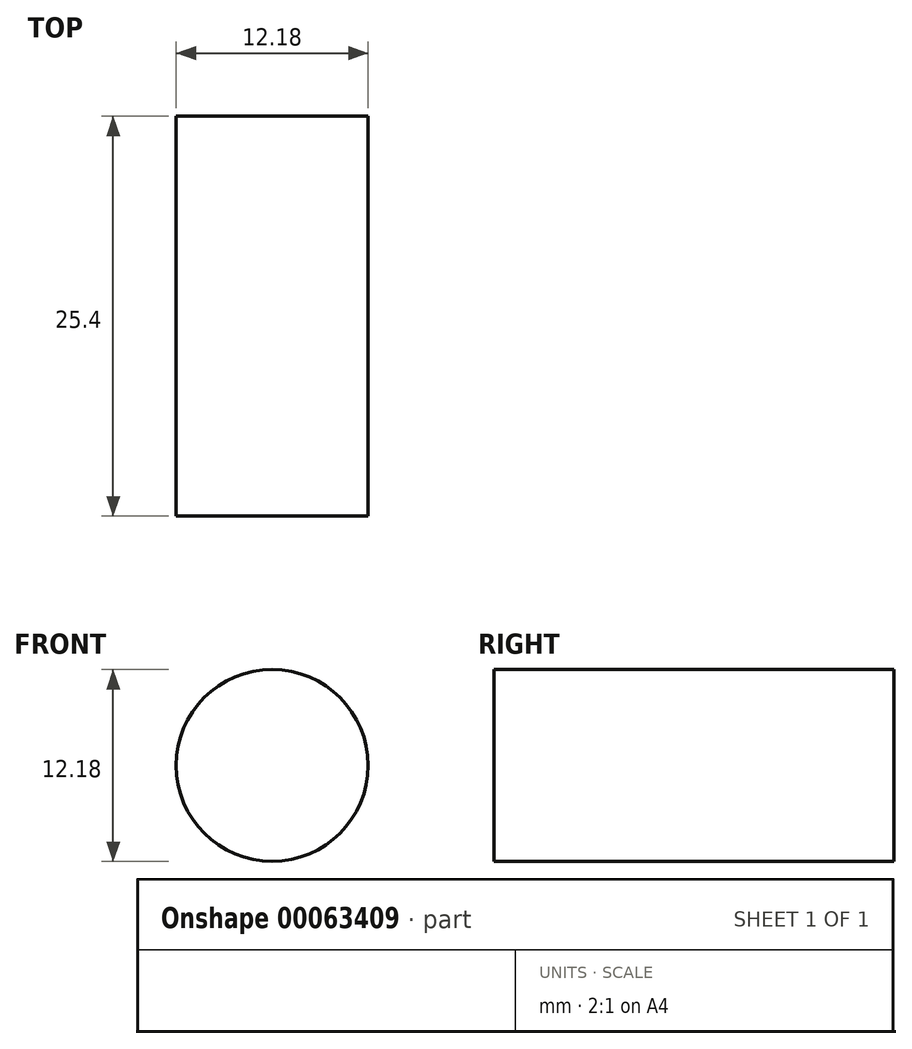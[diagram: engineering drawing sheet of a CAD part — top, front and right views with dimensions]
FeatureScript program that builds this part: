
annotation { "Feature Type Name" : "Feature", "Feature Type Description" : "" }
export const myFeature = defineFeature(function(context is Context, id is Id, definition is map)
    precondition{}
    {
        {
            var Q0;
            Q0=qCreatedBy(makeId("Front.planeOp"),FACE);
            var sketch = newSketch(context, id + "F0", { "sketchPlane" : qUnion([Q0])});
            skCircle(sketch, "E0", {"center": v(0, 0) * mm, "radius": 6.1 * mm});
            skSolve(sketch);
        }
        {
            var Q0;
            Q0 = qSketchRegion(id + "F0", true);
            extrude(context, id + "F1", {"entities" : qUnion([Q0]), "depth" : 25.4 * mm});
        }
    });
